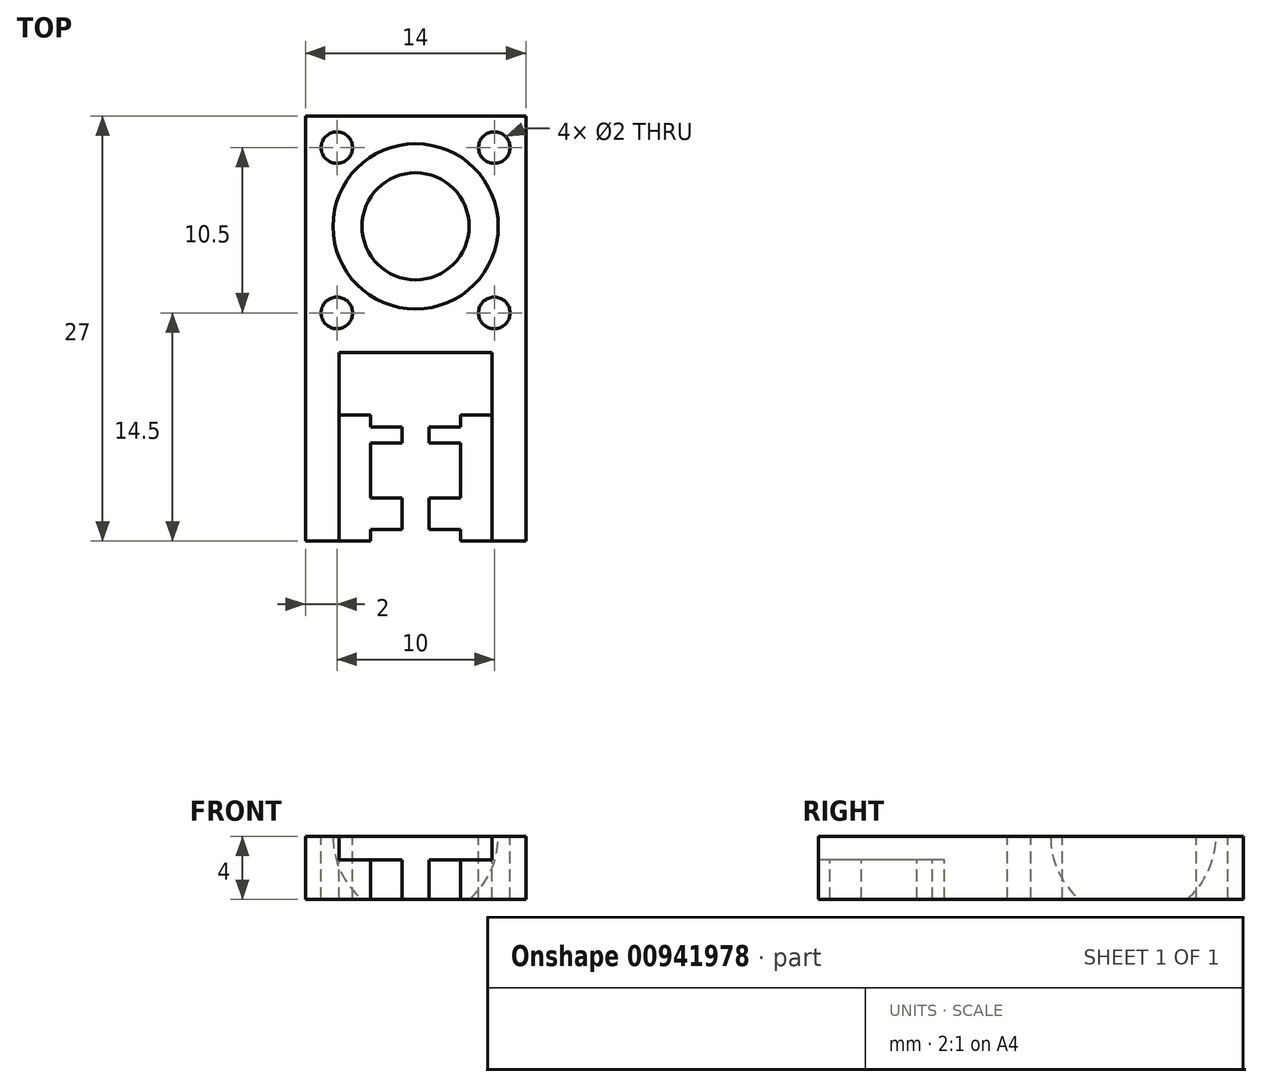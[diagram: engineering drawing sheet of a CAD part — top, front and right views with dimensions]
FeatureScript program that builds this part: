
annotation { "Feature Type Name" : "Feature", "Feature Type Description" : "" }
export const myFeature = defineFeature(function(context is Context, id is Id, definition is map)
    precondition{}
    {
        {
            var Q0;
            Q0=qCreatedBy(makeId("Top.planeOp"),FACE);
            var sketch = newSketch(context, id + "F0", { "sketchPlane" : qUnion([Q0])});
            skLineSegment(sketch, "E0.bottom", {"start": v(0, 0) * mm, "end": v(14, 0) * mm});
            skLineSegment(sketch, "E0.top", {"start": v(0, 27) * mm, "end": v(14, 27) * mm});
            skLineSegment(sketch, "E0.left", {"start": v(0, 0) * mm, "end": v(0, 27) * mm});
            skLineSegment(sketch, "E0.right", {"start": v(14, 0) * mm, "end": v(14, 27) * mm});
            skSolve(sketch);
        }
        {
            var Q0;
            Q0=makeQuery(id+"F0.imprint","IMPRINT",FACE,{"disambiguationData":[TD([[makeQuery(id+"F0.imprint","IMPRINT",EDGE,{"derivedFrom":sQuery(id+"F0.wireOp",EDGE,"E0.bottom")}),1.0]])]});
            extrude(context, id + "F1", {"entities" : qUnion([Q0]), "depth" : 4 * mm, "offsetDistance" : 25 * mm});
        }
        {
            var Q0;
            Q0=makeQuery(id+"F1.opExtrude","CAP_FACE",FACE,{"disambiguationData":[OSD([sQuery(id+"F0.wireOp",EDGE,"E0.bottom"),sQuery(id+"F0.wireOp",EDGE,"E0.top"),sQuery(id+"F0.wireOp",EDGE,"E0.left"),sQuery(id+"F0.wireOp",EDGE,"E0.right")])],"isStart":false});
            var sketch = newSketch(context, id + "F2", { "sketchPlane" : qUnion([Q0])});
            skLineSegment(sketch, "E1", {"start": v(7, 25.25) * mm, "end": v(7, 14.75) * mm});
            skArc(sketch, "E2", {"start": v(7, 14.75) * mm, "mid": v(12.25, 20) * mm, "end": v(7, 25.25) * mm});
            skLineSegment(sketch, "E3", {"start": v(0, 0) * mm, "end": v(0, 8) * mm});
            skLineSegment(sketch, "E4", {"start": v(0, 8) * mm, "end": v(4.15, 8) * mm});
            skLineSegment(sketch, "E5", {"start": v(4.15, 8) * mm, "end": v(4.15, 7.25) * mm});
            skLineSegment(sketch, "E6", {"start": v(4.15, 7.25) * mm, "end": v(6.15, 7.25) * mm});
            skLineSegment(sketch, "E7", {"start": v(6.15, 7.25) * mm, "end": v(6.15, 6.25) * mm});
            skLineSegment(sketch, "E8", {"start": v(6.15, 6.25) * mm, "end": v(4.15, 6.25) * mm});
            skLineSegment(sketch, "E9", {"start": v(4.15, 6.25) * mm, "end": v(4.15, 2.75) * mm});
            skLineSegment(sketch, "E10", {"start": v(4.15, 2.75) * mm, "end": v(6.15, 2.75) * mm});
            skLineSegment(sketch, "E11", {"start": v(6.15, 2.75) * mm, "end": v(6.15, 0.75) * mm});
            skLineSegment(sketch, "E12", {"start": v(6.15, 0.75) * mm, "end": v(4.15, 0.75) * mm});
            skLineSegment(sketch, "E13", {"start": v(4.15, 0.75) * mm, "end": v(4.15, 0) * mm});
            skLineSegment(sketch, "E14", {"start": v(0, 0) * mm, "end": v(4.15, 0) * mm});
            skLineSegment(sketch, "E15", {"start": v(14, 8) * mm, "end": v(9.85, 8) * mm});
            skLineSegment(sketch, "E16", {"start": v(9.85, 8) * mm, "end": v(9.85, 7.25) * mm});
            skLineSegment(sketch, "E17", {"start": v(9.85, 7.25) * mm, "end": v(7.85, 7.25) * mm});
            skLineSegment(sketch, "E18", {"start": v(7.85, 7.25) * mm, "end": v(7.85, 6.25) * mm});
            skLineSegment(sketch, "E19", {"start": v(7.85, 6.25) * mm, "end": v(9.85, 6.25) * mm});
            skLineSegment(sketch, "E20", {"start": v(9.85, 6.25) * mm, "end": v(9.85, 2.75) * mm});
            skLineSegment(sketch, "E21", {"start": v(9.85, 2.75) * mm, "end": v(7.85, 2.75) * mm});
            skLineSegment(sketch, "E22", {"start": v(7.85, 2.75) * mm, "end": v(7.85, 0.75) * mm});
            skLineSegment(sketch, "E23", {"start": v(7.85, 0.75) * mm, "end": v(9.85, 0.75) * mm});
            skLineSegment(sketch, "E24", {"start": v(9.85, 0.75) * mm, "end": v(9.85, 0) * mm});
            skLineSegment(sketch, "E25", {"start": v(9.85, 0) * mm, "end": v(14, 0) * mm});
            skLineSegment(sketch, "E26", {"start": v(14, 0) * mm, "end": v(14, 8) * mm});
            skLineSegment(sketch, "E27", {"start": v(0, 12) * mm, "end": v(14, 12) * mm});
            skCircle(sketch, "E28", {"center": v(12, 14.5) * mm, "radius": 1 * mm});
            skCircle(sketch, "E29", {"center": v(2, 25) * mm, "radius": 1 * mm});
            skLineSegment(sketch, "E30", {"start": v(11.85, 8) * mm, "end": v(11.85, 12) * mm});
            skLineSegment(sketch, "E31", {"start": v(2.15, 8) * mm, "end": v(2.15, 12) * mm});
            skLineSegment(sketch, "E32", {"start": v(2.15, 8) * mm, "end": v(2.15, 0) * mm});
            skLineSegment(sketch, "E33", {"start": v(11.85, 8) * mm, "end": v(11.85, 0) * mm});
            skCircle(sketch, "E34", {"center": v(12, 25) * mm, "radius": 1 * mm});
            skCircle(sketch, "E35", {"center": v(2, 14.5) * mm, "radius": 1 * mm});
            skSolve(sketch);
        }
        {
            var Q0;
            Q0=makeQuery(id+"F2.imprint","IMPRINT",FACE,{"disambiguationData":[TD([[makeQuery(id+"F2.imprint","IMPRINT",EDGE,{"derivedFrom":sQuery(id+"F2.wireOp",EDGE,"E1")}),1.0]])]});
            var Q1;
            Q1=sQuery(id+"F2.wireOp",EDGE,"E1");
            revolve(context, id + "F3", {"operationType" : NewBodyOperationType.REMOVE, "surfaceOperationType" : NewSurfaceOperationType.NEW, "entities" : qUnion([Q0]), "axis" : qUnion([Q1]), "revolveType" : RevolveType.FULL, "oppositeDirection" : true});
        }
        {
            var Q0;
            Q0=makeQuery(id+"F2.imprint","IMPRINT",FACE,{"disambiguationData":[TD([[makeQuery(id+"F2.imprint","IMPRINT",EDGE,{"derivedFrom":sQuery(id+"F2.wireOp",EDGE,"E29")}),1.0]])]});
            var Q1;
            Q1=makeQuery(id+"F2.imprint","IMPRINT",FACE,{"disambiguationData":[TD([[makeQuery(id+"F2.imprint","IMPRINT",EDGE,{"derivedFrom":sQuery(id+"F2.wireOp",EDGE,"E28")}),1.0]])]});
            var Q2;
            Q2=makeQuery(id+"F2.imprint","IMPRINT",FACE,{"disambiguationData":[TD([[makeQuery(id+"F2.imprint","IMPRINT",EDGE,{"derivedFrom":sQuery(id+"F2.wireOp",EDGE,"E34")}),1.0]])]});
            var Q3;
            Q3=makeQuery(id+"F2.imprint","IMPRINT",FACE,{"disambiguationData":[TD([[makeQuery(id+"F2.imprint","IMPRINT",EDGE,{"derivedFrom":sQuery(id+"F2.wireOp",EDGE,"E35")}),1.0]])]});
            extrude(context, id + "F4", {"entities" : qUnion([Q0, Q1, Q2, Q3]), "operationType" : NewBodyOperationType.REMOVE, "oppositeDirection" : true, "depth" : 4 * mm, "offsetDistance" : 25 * mm});
        }
        {
            var Q0;
            {var subQ6=sQuery(id+"F2.wireOp",EDGE,"E5");Q0=makeQuery(id+"F2.imprint","IMPRINT",FACE,{"disambiguationData":[TD([[makeQuery(id+"F2.imprint","IMPRINT",EDGE,{"derivedFrom":subQ6}),1.0]])]});}
            extrude(context, id + "F5", {"entities" : qUnion([Q0]), "operationType" : NewBodyOperationType.REMOVE, "oppositeDirection" : true, "depth" : 4 * mm, "offsetDistance" : 25 * mm});
        }
        {
            var Q0;
            {var subQ1=sQuery(id+"F2.wireOp",EDGE,"E5");Q0=makeQuery(id+"F2.imprint","IMPRINT",FACE,{"disambiguationData":[TD([[makeQuery(id+"F2.imprint","IMPRINT",EDGE,{"derivedFrom":subQ1}),-1.0]])]});}
            var Q1;
            {var subQ1=sQuery(id+"F2.wireOp",EDGE,"E16");Q1=makeQuery(id+"F2.imprint","IMPRINT",FACE,{"disambiguationData":[TD([[makeQuery(id+"F2.imprint","IMPRINT",EDGE,{"derivedFrom":subQ1}),1.0]])]});}
            extrude(context, id + "F6", {"entities" : qUnion([Q0, Q1]), "operationType" : NewBodyOperationType.REMOVE, "oppositeDirection" : true, "depth" : 1.5 * mm, "offsetDistance" : 25 * mm});
        }
    });
